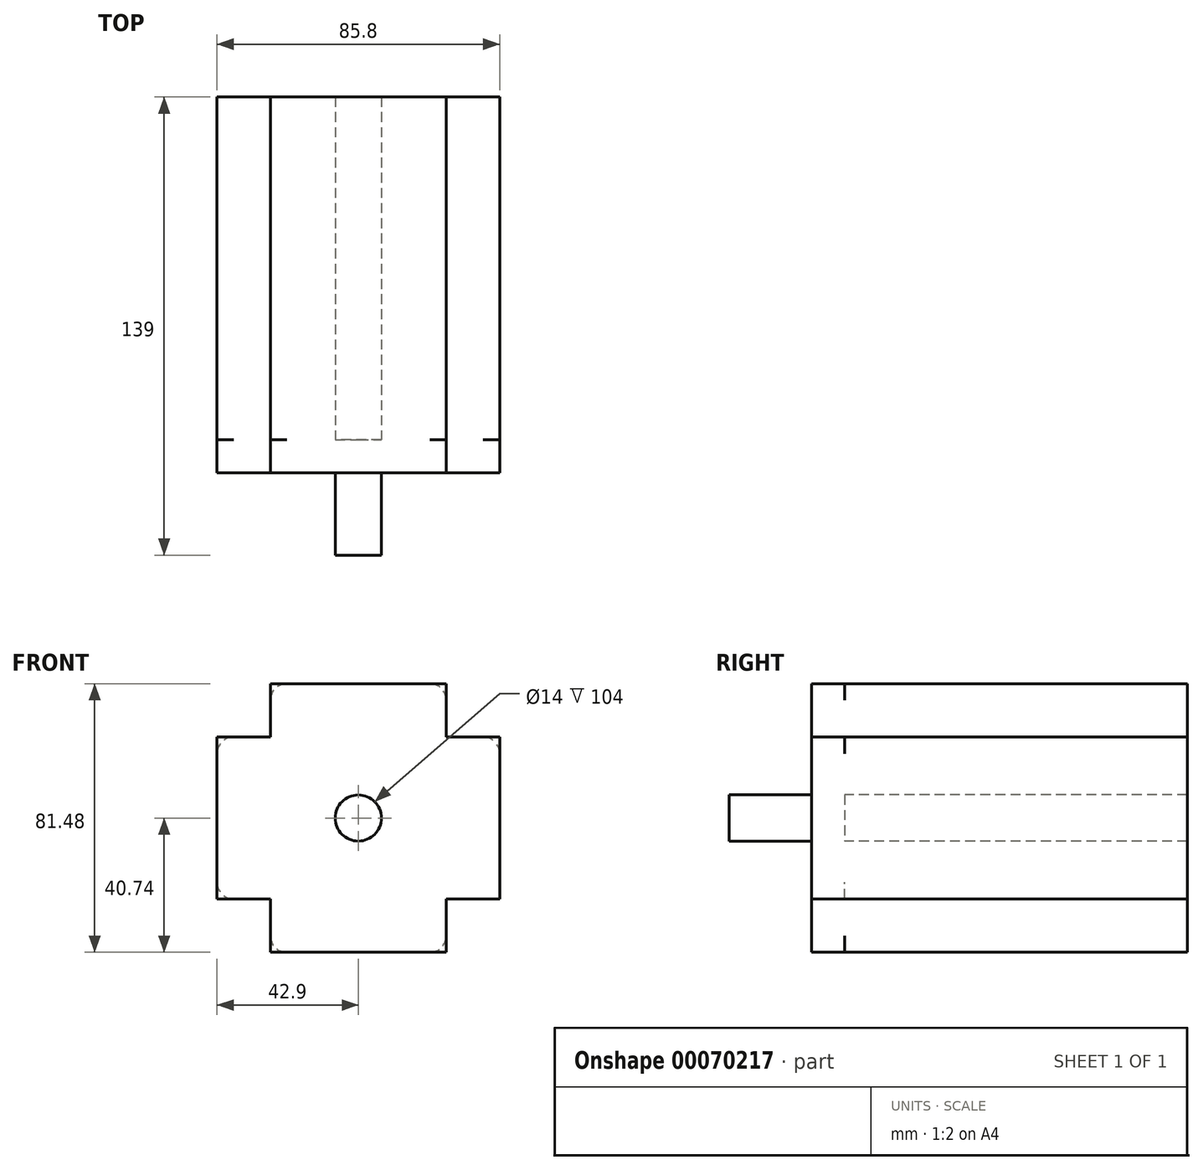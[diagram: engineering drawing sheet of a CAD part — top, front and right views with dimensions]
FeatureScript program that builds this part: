
annotation { "Feature Type Name" : "Feature", "Feature Type Description" : "" }
export const myFeature = defineFeature(function(context is Context, id is Id, definition is map)
    precondition{}
    {
        {
            var Q0;
            Q0=qCreatedBy(makeId("Front.planeOp"),FACE);
            var sketch = newSketch(context, id + "F0", { "sketchPlane" : qUnion([Q0])});
            skLineSegment(sketch, "E0.rect.bottom", {"start": v(42.9, -40.74) * mm, "end": v(-42.9, -40.74) * mm});
            skLineSegment(sketch, "E0.rect.top", {"start": v(42.9, 40.74) * mm, "end": v(-42.9, 40.74) * mm});
            skLineSegment(sketch, "E0.rect.left", {"start": v(42.9, -40.74) * mm, "end": v(42.9, 40.74) * mm});
            skLineSegment(sketch, "E0.rect.right", {"start": v(-42.9, -35.74) * mm, "end": v(-42.9, 40.74) * mm});
            skPoint(sketch, "E0.rect.middle", {"position": v(0, 0) * mm});
            skLineSegment(sketch, "E1.bottom", {"start": v(37.9, 40.74) * mm, "end": v(26.7, 40.74) * mm});
            skLineSegment(sketch, "E1.top", {"start": v(42.9, 24.54) * mm, "end": v(26.7, 24.54) * mm});
            skLineSegment(sketch, "E1.left", {"start": v(42.9, 35.74) * mm, "end": v(42.9, 24.54) * mm});
            skLineSegment(sketch, "E1.right", {"start": v(26.7, 40.74) * mm, "end": v(26.7, 24.54) * mm});
            skLineSegment(sketch, "E2.bottom", {"start": v(-37.9, 40.74) * mm, "end": v(-26.7, 40.74) * mm});
            skLineSegment(sketch, "E2.top", {"start": v(-42.9, 24.54) * mm, "end": v(-26.7, 24.54) * mm});
            skLineSegment(sketch, "E2.left", {"start": v(-42.9, 35.74) * mm, "end": v(-42.9, 24.54) * mm});
            skLineSegment(sketch, "E2.right", {"start": v(-26.7, 40.74) * mm, "end": v(-26.7, 24.54) * mm});
            skLineSegment(sketch, "E3.bottom", {"start": v(-37.9, -40.74) * mm, "end": v(-26.7, -40.74) * mm});
            skLineSegment(sketch, "E3.top", {"start": v(-42.9, -24.54) * mm, "end": v(-26.7, -24.54) * mm});
            skLineSegment(sketch, "E3.left", {"start": v(-42.9, -40.74) * mm, "end": v(-42.9, -24.54) * mm});
            skLineSegment(sketch, "E3.right", {"start": v(-26.7, -40.74) * mm, "end": v(-26.7, -24.54) * mm});
            skLineSegment(sketch, "E4.bottom", {"start": v(37.9, -40.74) * mm, "end": v(26.7, -40.74) * mm});
            skLineSegment(sketch, "E4.top", {"start": v(42.9, -24.54) * mm, "end": v(26.7, -24.54) * mm});
            skLineSegment(sketch, "E4.left", {"start": v(42.9, -35.74) * mm, "end": v(42.9, -24.54) * mm});
            skLineSegment(sketch, "E4.right", {"start": v(26.7, -40.74) * mm, "end": v(26.7, -24.54) * mm});
            skCircle(sketch, "E5", {"center": v(0, 0) * mm, "radius": 30 * mm});
            skCircle(sketch, "E6", {"center": v(0, 0) * mm, "radius": 7 * mm});
            skCircle(sketch, "E7", {"center": v(-34.8, 32.64) * mm, "radius": 3.25 * mm});
            skPoint(sketch, "E7.centerSnap0", {"position": v(-34.8, 40.74) * mm});
            skPoint(sketch, "E7.centerSnap1", {"position": v(-26.7, 32.64) * mm});
            skCircle(sketch, "E8", {"center": v(34.8, 32.64) * mm, "radius": 3.25 * mm});
            skPoint(sketch, "E8.centerSnap0", {"position": v(42.9, 32.64) * mm});
            skPoint(sketch, "E8.centerSnap1", {"position": v(34.8, 40.74) * mm});
            skCircle(sketch, "E9", {"center": v(34.8, -32.64) * mm, "radius": 3.25 * mm});
            skPoint(sketch, "E9.centerSnap0", {"position": v(42.9, -32.64) * mm});
            skPoint(sketch, "E9.centerSnap1", {"position": v(34.8, -24.54) * mm});
            skCircle(sketch, "E10", {"center": v(-34.8, -32.64) * mm, "radius": 3.25 * mm});
            skPoint(sketch, "E10.centerSnap0", {"position": v(-26.7, -32.64) * mm});
            skPoint(sketch, "E10.centerSnap1", {"position": v(-34.8, -24.54) * mm});
            skPoint(sketch, "E11.visualSharp", {"position": v(-42.9, 40.74) * mm});
            skArc(sketch, "E11.filletArc", {"start": v(-37.9, 40.74) * mm, "mid": v(-41.44, 39.27) * mm, "end": v(-42.9, 35.74) * mm});
            skPoint(sketch, "E12.visualSharp", {"position": v(42.9, 40.74) * mm});
            skArc(sketch, "E12.filletArc", {"start": v(42.9, 35.74) * mm, "mid": v(41.44, 39.27) * mm, "end": v(37.9, 40.74) * mm});
            skPoint(sketch, "E13.visualSharp", {"position": v(42.9, -40.74) * mm});
            skArc(sketch, "E13.filletArc", {"start": v(37.9, -40.74) * mm, "mid": v(41.44, -39.27) * mm, "end": v(42.9, -35.74) * mm});
            skPoint(sketch, "E14.visualSharp", {"position": v(-42.9, -40.74) * mm});
            skArc(sketch, "E14.filletArc", {"start": v(-42.9, -35.74) * mm, "mid": v(-41.44, -39.27) * mm, "end": v(-37.9, -40.74) * mm});
            skSolve(sketch);
        }
        {
            var Q0;
            Q0=makeQuery(id+"F0.imprint","IMPRINT",FACE,{"disambiguationData":[TD([[makeQuery(id+"F0.imprint","IMPRINT",EDGE,{"derivedFrom":sQuery(id+"F0.wireOp",EDGE,"E2.bottom")}),-1.0]])]});
            var Q1;
            Q1=makeQuery(id+"F0.imprint","IMPRINT",FACE,{"disambiguationData":[TD([[makeQuery(id+"F0.imprint","IMPRINT",EDGE,{"derivedFrom":sQuery(id+"F0.wireOp",EDGE,"E7")}),1.0]])]});
            var Q2;
            {var subQ3=sQuery(id+"F0.wireOp",EDGE,"E1.top");Q2=makeQuery(id+"F0.imprint","IMPRINT",FACE,{"disambiguationData":[TD([[makeQuery(id+"F0.imprint","IMPRINT",EDGE,{"derivedFrom":subQ3}),1.0]])]});}
            var Q3;
            Q3=makeQuery(id+"F0.imprint","IMPRINT",FACE,{"disambiguationData":[TD([[makeQuery(id+"F0.imprint","IMPRINT",EDGE,{"derivedFrom":sQuery(id+"F0.wireOp",EDGE,"E1.bottom")}),1.0]])]});
            var Q4;
            Q4=makeQuery(id+"F0.imprint","IMPRINT",FACE,{"disambiguationData":[TD([[makeQuery(id+"F0.imprint","IMPRINT",EDGE,{"derivedFrom":sQuery(id+"F0.wireOp",EDGE,"E8")}),1.0]])]});
            var Q5;
            Q5=makeQuery(id+"F0.imprint","IMPRINT",FACE,{"disambiguationData":[TD([[makeQuery(id+"F0.imprint","IMPRINT",EDGE,{"derivedFrom":sQuery(id+"F0.wireOp",EDGE,"E5")}),1.0]])]});
            var Q6;
            Q6=makeQuery(id+"F0.imprint","IMPRINT",FACE,{"disambiguationData":[TD([[makeQuery(id+"F0.imprint","IMPRINT",EDGE,{"derivedFrom":sQuery(id+"F0.wireOp",EDGE,"E6")}),1.0]])]});
            var Q7;
            Q7=makeQuery(id+"F0.imprint","IMPRINT",FACE,{"disambiguationData":[TD([[makeQuery(id+"F0.imprint","IMPRINT",EDGE,{"derivedFrom":sQuery(id+"F0.wireOp",EDGE,"E10")}),1.0]])]});
            var Q8;
            Q8=makeQuery(id+"F0.imprint","IMPRINT",FACE,{"disambiguationData":[TD([[makeQuery(id+"F0.imprint","IMPRINT",EDGE,{"derivedFrom":sQuery(id+"F0.wireOp",EDGE,"E3.bottom")}),1.0]])]});
            var Q9;
            Q9=makeQuery(id+"F0.imprint","IMPRINT",FACE,{"disambiguationData":[TD([[makeQuery(id+"F0.imprint","IMPRINT",EDGE,{"derivedFrom":sQuery(id+"F0.wireOp",EDGE,"E4.bottom")}),-1.0]])]});
            var Q10;
            Q10=makeQuery(id+"F0.imprint","IMPRINT",FACE,{"disambiguationData":[TD([[makeQuery(id+"F0.imprint","IMPRINT",EDGE,{"derivedFrom":sQuery(id+"F0.wireOp",EDGE,"E9")}),1.0]])]});
            extrude(context, id + "F1", {"entities" : qUnion([Q0, Q1, Q2, Q3, Q4, Q5, Q6, Q7, Q8, Q9, Q10]), "oppositeDirection" : true, "depth" : 10 * mm});
        }
        {
            var Q0;
            Q0=makeQuery(id+"F1.opExtrude","CAP_FACE",FACE,{"disambiguationData":[OSD([sQuery(id+"F0.wireOp",EDGE,"E0.rect.bottom"),sQuery(id+"F0.wireOp",EDGE,"E0.rect.top"),sQuery(id+"F0.wireOp",EDGE,"E0.rect.left"),sQuery(id+"F0.wireOp",EDGE,"E0.rect.right"),sQuery(id+"F0.wireOp",EDGE,"E1.bottom"),sQuery(id+"F0.wireOp",EDGE,"E1.left"),sQuery(id+"F0.wireOp",EDGE,"E2.bottom"),sQuery(id+"F0.wireOp",EDGE,"E2.left"),sQuery(id+"F0.wireOp",EDGE,"E3.bottom"),sQuery(id+"F0.wireOp",EDGE,"E3.left"),sQuery(id+"F0.wireOp",EDGE,"E4.bottom"),sQuery(id+"F0.wireOp",EDGE,"E4.left"),sQuery(id+"F0.wireOp",EDGE,"E11.filletArc"),sQuery(id+"F0.wireOp",EDGE,"E12.filletArc"),sQuery(id+"F0.wireOp",EDGE,"E13.filletArc"),sQuery(id+"F0.wireOp",EDGE,"E14.filletArc")])],"isStart":false});
            var sketch = newSketch(context, id + "F2", { "sketchPlane" : qUnion([Q0])});
            skLineSegment(sketch, "E15.0", {"start": v(-21.7, -40.74) * mm, "end": v(21.7, -40.74) * mm});
            skLineSegment(sketch, "E15.1", {"start": v(-21.7, 40.74) * mm, "end": v(21.7, 40.74) * mm});
            skLineSegment(sketch, "E15.2", {"start": v(-42.9, -40.74) * mm, "end": v(-42.9, 19.54) * mm});
            skLineSegment(sketch, "E15.3", {"start": v(42.9, -19.54) * mm, "end": v(42.9, 19.54) * mm});
            skPoint(sketch, "E15.4", {"position": v(0, 0) * mm});
            skLineSegment(sketch, "E15.5", {"start": v(-37.9, 40.74) * mm, "end": v(-26.7, 40.74) * mm});
            skLineSegment(sketch, "E15.6", {"start": v(-37.9, 24.54) * mm, "end": v(-31.7, 24.54) * mm});
            skLineSegment(sketch, "E15.7", {"start": v(-42.9, 35.74) * mm, "end": v(-42.9, 24.54) * mm});
            skLineSegment(sketch, "E15.8", {"start": v(-26.7, 35.74) * mm, "end": v(-26.7, 29.54) * mm});
            skLineSegment(sketch, "E15.9", {"start": v(37.9, 40.74) * mm, "end": v(26.7, 40.74) * mm});
            skLineSegment(sketch, "E15.10", {"start": v(37.9, 24.54) * mm, "end": v(31.7, 24.54) * mm});
            skLineSegment(sketch, "E15.11", {"start": v(42.9, 35.74) * mm, "end": v(42.9, 24.54) * mm});
            skLineSegment(sketch, "E15.12", {"start": v(26.7, 35.74) * mm, "end": v(26.7, 29.54) * mm});
            skLineSegment(sketch, "E15.13", {"start": v(37.9, -40.74) * mm, "end": v(26.7, -40.74) * mm});
            skLineSegment(sketch, "E15.14", {"start": v(37.9, -24.54) * mm, "end": v(31.7, -24.54) * mm});
            skLineSegment(sketch, "E15.15", {"start": v(42.9, -40.74) * mm, "end": v(42.9, -24.54) * mm});
            skLineSegment(sketch, "E15.16", {"start": v(26.7, -35.74) * mm, "end": v(26.7, -29.54) * mm});
            skLineSegment(sketch, "E15.17", {"start": v(-37.9, -40.74) * mm, "end": v(-26.7, -40.74) * mm});
            skLineSegment(sketch, "E15.18", {"start": v(-42.9, -24.54) * mm, "end": v(-31.7, -24.54) * mm});
            skLineSegment(sketch, "E15.19", {"start": v(-42.9, -35.74) * mm, "end": v(-42.9, -24.54) * mm});
            skLineSegment(sketch, "E15.20", {"start": v(-26.7, -35.74) * mm, "end": v(-26.7, -29.54) * mm});
            skCircle(sketch, "E15.21", {"center": v(0, 0) * mm, "radius": 30 * mm});
            skCircle(sketch, "E15.22", {"center": v(0, 0) * mm, "radius": 7 * mm});
            skCircle(sketch, "E15.23", {"center": v(34.8, 32.64) * mm, "radius": 3.25 * mm});
            skPoint(sketch, "E15.24", {"position": v(34.8, 40.74) * mm});
            skPoint(sketch, "E15.25", {"position": v(26.7, 32.64) * mm});
            skCircle(sketch, "E15.26", {"center": v(-34.8, 32.64) * mm, "radius": 3.25 * mm});
            skPoint(sketch, "E15.27", {"position": v(-42.9, 32.64) * mm});
            skPoint(sketch, "E15.28", {"position": v(-34.8, 40.74) * mm});
            skCircle(sketch, "E15.29", {"center": v(-34.8, -32.64) * mm, "radius": 3.25 * mm});
            skPoint(sketch, "E15.30", {"position": v(-42.9, -32.64) * mm});
            skPoint(sketch, "E15.31", {"position": v(-34.8, -24.54) * mm});
            skCircle(sketch, "E15.32", {"center": v(34.8, -32.64) * mm, "radius": 3.25 * mm});
            skPoint(sketch, "E15.33", {"position": v(26.7, -32.64) * mm});
            skPoint(sketch, "E15.34", {"position": v(34.8, -24.54) * mm});
            skPoint(sketch, "E15.35", {"position": v(42.9, 40.74) * mm});
            skArc(sketch, "E15.36", {"start": v(37.9, 40.74) * mm, "mid": v(41.44, 39.27) * mm, "end": v(42.9, 35.74) * mm});
            skPoint(sketch, "E15.37", {"position": v(-42.9, 40.74) * mm});
            skArc(sketch, "E15.38", {"start": v(-42.9, 35.74) * mm, "mid": v(-41.44, 39.27) * mm, "end": v(-37.9, 40.74) * mm});
            skPoint(sketch, "E15.39", {"position": v(-42.9, -40.74) * mm});
            skArc(sketch, "E15.40", {"start": v(-37.9, -40.74) * mm, "mid": v(-41.44, -39.27) * mm, "end": v(-42.9, -35.74) * mm});
            skPoint(sketch, "E15.41", {"position": v(42.9, -40.74) * mm});
            skArc(sketch, "E15.42", {"start": v(42.9, -35.74) * mm, "mid": v(41.44, -39.27) * mm, "end": v(37.9, -40.74) * mm});
            skPoint(sketch, "E16.visualSharp", {"position": v(-26.7, 24.54) * mm});
            skArc(sketch, "E16.filletArc", {"start": v(-31.7, 24.54) * mm, "mid": v(-28.16, 26) * mm, "end": v(-26.7, 29.54) * mm});
            skPoint(sketch, "E17.visualSharp", {"position": v(26.7, 24.54) * mm});
            skArc(sketch, "E17.filletArc", {"start": v(26.7, 29.54) * mm, "mid": v(28.16, 26) * mm, "end": v(31.7, 24.54) * mm});
            skPoint(sketch, "E18.visualSharp", {"position": v(-26.7, -24.54) * mm});
            skArc(sketch, "E18.filletArc", {"start": v(-26.7, -29.54) * mm, "mid": v(-28.16, -26) * mm, "end": v(-31.7, -24.54) * mm});
            skPoint(sketch, "E19.visualSharp", {"position": v(26.7, -24.54) * mm});
            skArc(sketch, "E19.filletArc", {"start": v(31.7, -24.54) * mm, "mid": v(28.16, -26) * mm, "end": v(26.7, -29.54) * mm});
            skPoint(sketch, "E20.newPointA", {"position": v(-26.7, 40.74) * mm});
            skArc(sketch, "E20.filletArc", {"start": v(-21.7, 40.74) * mm, "mid": v(-25.24, 39.27) * mm, "end": v(-26.7, 35.74) * mm});
            skPoint(sketch, "E21.newPointA", {"position": v(-42.9, 24.54) * mm});
            skArc(sketch, "E21.filletArc", {"start": v(-37.9, 24.54) * mm, "mid": v(-41.44, 23.07) * mm, "end": v(-42.9, 19.54) * mm});
            skPoint(sketch, "E22.newPointA", {"position": v(26.7, 40.74) * mm});
            skArc(sketch, "E22.filletArc", {"start": v(26.7, 35.74) * mm, "mid": v(25.24, 39.27) * mm, "end": v(21.7, 40.74) * mm});
            skPoint(sketch, "E23.newPointA", {"position": v(42.9, 24.54) * mm});
            skArc(sketch, "E23.filletArc", {"start": v(42.9, 19.54) * mm, "mid": v(41.44, 23.07) * mm, "end": v(37.9, 24.54) * mm});
            skPoint(sketch, "E24.newPointA", {"position": v(42.9, -24.54) * mm});
            skPoint(sketch, "E24.newPointB", {"position": v(42.9, -35.74) * mm});
            skArc(sketch, "E24.filletArc", {"start": v(37.9, -24.54) * mm, "mid": v(41.44, -23.07) * mm, "end": v(42.9, -19.54) * mm});
            skPoint(sketch, "E25.newPointA", {"position": v(26.7, -40.74) * mm});
            skArc(sketch, "E25.filletArc", {"start": v(21.7, -40.74) * mm, "mid": v(25.24, -39.27) * mm, "end": v(26.7, -35.74) * mm});
            skPoint(sketch, "E26.newPointA", {"position": v(-26.7, -40.74) * mm});
            skArc(sketch, "E26.filletArc", {"start": v(-26.7, -35.74) * mm, "mid": v(-25.24, -39.27) * mm, "end": v(-21.7, -40.74) * mm});
            skSolve(sketch);
        }
        {
            var Q0;
            Q0=makeQuery(id+"F2.imprint","IMPRINT",FACE,{"disambiguationData":[TD([[makeQuery(id+"F2.imprint","IMPRINT",EDGE,{"derivedFrom":sQuery(id+"F2.wireOp",EDGE,"E15.0")}),1.0]])]});
            var Q1;
            Q1=makeQuery(id+"F2.imprint","IMPRINT",FACE,{"disambiguationData":[TD([[makeQuery(id+"F2.imprint","IMPRINT",EDGE,{"derivedFrom":sQuery(id+"F2.wireOp",EDGE,"E15.21")}),-1.0]])]});
            var Q2;
            Q2=makeQuery(id+"F2.imprint","IMPRINT",FACE,{"disambiguationData":[TD([[makeQuery(id+"F2.imprint","IMPRINT",EDGE,{"derivedFrom":sQuery(id+"F2.wireOp",EDGE,"E15.22")}),-1.0]])]});
            extrude(context, id + "F3", {"entities" : qUnion([Q0, Q1, Q2]), "operationType" : NewBodyOperationType.ADD, "depth" : 104 * mm});
        }
        {
            var Q0;
            Q0=makeQuery(id+"F0.imprint","IMPRINT",FACE,{"disambiguationData":[TD([[makeQuery(id+"F0.imprint","IMPRINT",EDGE,{"derivedFrom":sQuery(id+"F0.wireOp",EDGE,"E8")}),1.0]])]});
            var Q1;
            Q1=makeQuery(id+"F0.imprint","IMPRINT",FACE,{"disambiguationData":[TD([[makeQuery(id+"F0.imprint","IMPRINT",EDGE,{"derivedFrom":sQuery(id+"F0.wireOp",EDGE,"E7")}),1.0]])]});
            var Q2;
            Q2=makeQuery(id+"F0.imprint","IMPRINT",FACE,{"disambiguationData":[TD([[makeQuery(id+"F0.imprint","IMPRINT",EDGE,{"derivedFrom":sQuery(id+"F0.wireOp",EDGE,"E10")}),1.0]])]});
            var Q3;
            Q3=makeQuery(id+"F0.imprint","IMPRINT",FACE,{"disambiguationData":[TD([[makeQuery(id+"F0.imprint","IMPRINT",EDGE,{"derivedFrom":sQuery(id+"F0.wireOp",EDGE,"E9")}),1.0]])]});
            extrude(context, id + "F4", {"entities" : qUnion([Q0, Q1, Q2, Q3]), "operationType" : NewBodyOperationType.REMOVE, "endBound" : BoundingType.THROUGH_ALL, "oppositeDirection" : true, "depth" : 25 * mm});
        }
        {
            var Q0;
            Q0=makeQuery(id+"F0.imprint","IMPRINT",FACE,{"disambiguationData":[TD([[makeQuery(id+"F0.imprint","IMPRINT",EDGE,{"derivedFrom":sQuery(id+"F0.wireOp",EDGE,"E6")}),1.0]])]});
            extrude(context, id + "F5", {"entities" : qUnion([Q0]), "depth" : 25 * mm});
        }
    });
